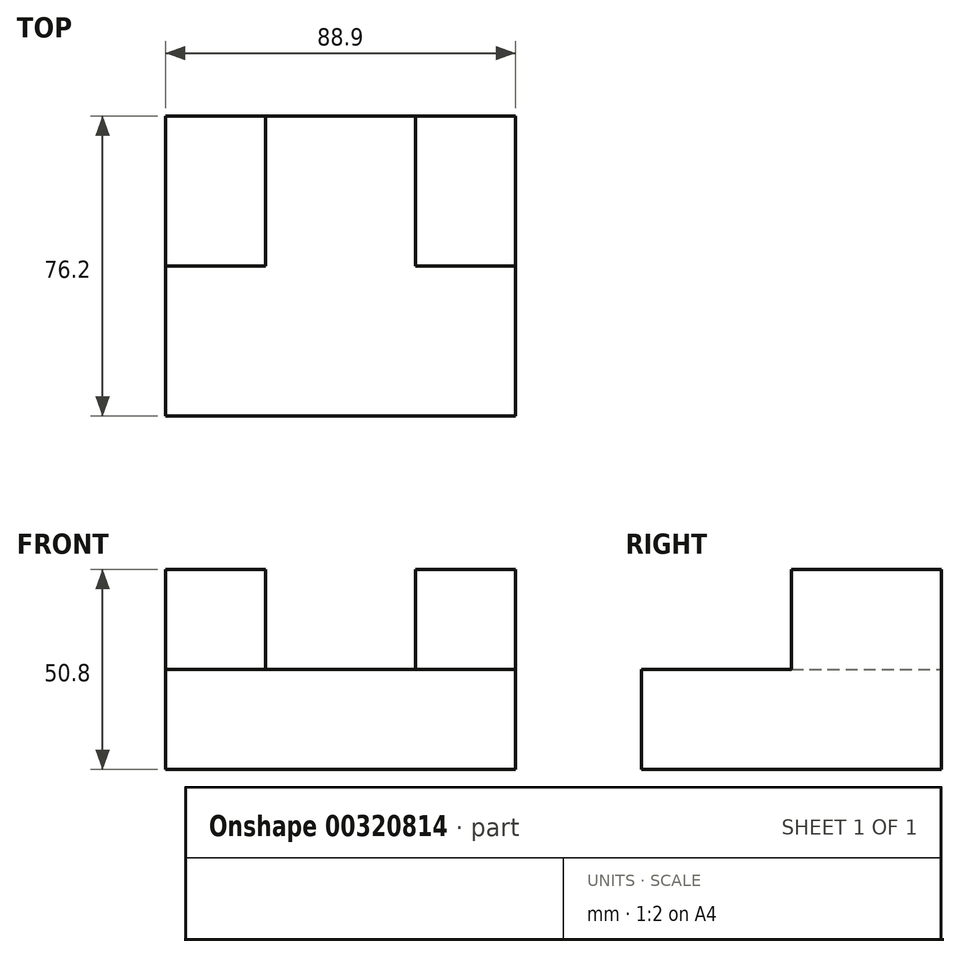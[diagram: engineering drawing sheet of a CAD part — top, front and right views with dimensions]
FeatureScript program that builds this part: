
annotation { "Feature Type Name" : "Feature", "Feature Type Description" : "" }
export const myFeature = defineFeature(function(context is Context, id is Id, definition is map)
    precondition{}
    {
        {
            var Q0;
            Q0=qCreatedBy(makeId("Right.planeOp"),FACE);
            var sketch = newSketch(context, id + "F0", { "sketchPlane" : qUnion([Q0])});
            skLineSegment(sketch, "E0", {"start": v(-45.25, -30.34) * mm, "end": v(30.95, -30.34) * mm});
            skLineSegment(sketch, "E1", {"start": v(30.95, -30.34) * mm, "end": v(30.95, 20.46) * mm});
            skLineSegment(sketch, "E2", {"start": v(30.95, 20.46) * mm, "end": v(-7.15, 20.46) * mm});
            skLineSegment(sketch, "E3", {"start": v(-7.15, 20.46) * mm, "end": v(-7.15, -4.94) * mm});
            skLineSegment(sketch, "E4", {"start": v(-7.15, -4.94) * mm, "end": v(-45.25, -4.94) * mm});
            skLineSegment(sketch, "E5", {"start": v(-45.25, -4.94) * mm, "end": v(-45.25, -30.34) * mm});
            skSolve(sketch);
        }
        {
            var Q0;
            Q0=makeQuery(id+"F0.imprint","IMPRINT",FACE,{"disambiguationData":[TD([[makeQuery(id+"F0.imprint","IMPRINT",EDGE,{"derivedFrom":sQuery(id+"F0.wireOp",EDGE,"E0")}),1.0]])]});
            extrude(context, id + "F1", {"entities" : qUnion([Q0]), "oppositeDirection" : true, "depth" : 88.9 * mm});
        }
        {
            var Q0;
            Q0=makeQuery(id+"F1.opExtrude","SWEPT_FACE",FACE,{"disambiguationData":[OSD([sQuery(id+"F0.wireOp",EDGE,"E3")])]});
            var sketch = newSketch(context, id + "F2", { "sketchPlane" : qUnion([Q0])});
            skLineSegment(sketch, "E6", {"start": v(-58.4, 20.46) * mm, "end": v(-58.4, -4.94) * mm});
            skLineSegment(sketch, "E7", {"start": v(-58.4, -4.94) * mm, "end": v(-20.3, -4.94) * mm});
            skLineSegment(sketch, "E8", {"start": v(-20.3, -4.94) * mm, "end": v(-21.07, 20.46) * mm});
            skLineSegment(sketch, "E9", {"start": v(-58.4, 20.46) * mm, "end": v(-21.07, 20.46) * mm});
            skSolve(sketch);
        }
        {
            var Q0;
            Q0=makeQuery(id+"F1.opExtrude","SWEPT_FACE",FACE,{"disambiguationData":[OSD([sQuery(id+"F0.wireOp",EDGE,"E2")])]});
            var sketch = newSketch(context, id + "F3", { "sketchPlane" : qUnion([Q0])});
            skLineSegment(sketch, "E10", {"start": v(-63.5, 11.9) * mm, "end": v(-63.5, -7.15) * mm});
            skLineSegment(sketch, "E11", {"start": v(-63.5, -7.15) * mm, "end": v(-25.4, -7.15) * mm});
            skLineSegment(sketch, "E12", {"start": v(-25.4, -7.15) * mm, "end": v(-25.4, 30.95) * mm});
            skLineSegment(sketch, "E13", {"start": v(-25.4, 30.95) * mm, "end": v(-63.5, 30.95) * mm});
            skLineSegment(sketch, "E14", {"start": v(-63.5, 30.95) * mm, "end": v(-63.5, 11.9) * mm});
            skSolve(sketch);
        }
        {
            var Q0;
            Q0=makeQuery(id+"F3.imprint","IMPRINT",FACE,{"disambiguationData":[TD([[makeQuery(id+"F3.imprint","IMPRINT",EDGE,{"derivedFrom":sQuery(id+"F3.wireOp",EDGE,"E10")}),1.0]])]});
            extrude(context, id + "F4", {"entities" : qUnion([Q0]), "operationType" : NewBodyOperationType.REMOVE, "oppositeDirection" : true, "depth" : 25.4 * mm});
        }
    });
